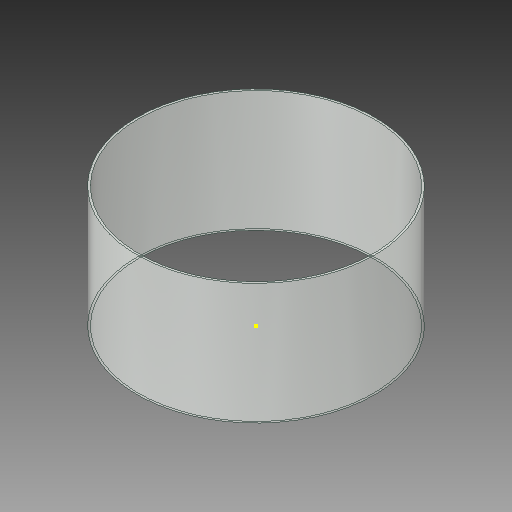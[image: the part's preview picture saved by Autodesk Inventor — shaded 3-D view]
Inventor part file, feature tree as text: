
AUTODESK INVENTOR PART (.ipt)
format: ipt  version: 2019 (Build 230136000, 136)  size: 118,272 bytes
history: native  units: mm
features: sketch x3, extrude x1
ambient origin geometry x8: Origin, YZ Plane, XZ Plane, XY Plane, X Axis, Y Axis, Z Axis, Center Point
bodies: Solid1 (feature_tree)
feature tree (4):
  sketch  "Sketch1"  dims[d0=305.0mm d1=300.0mm]
  extrude  "Extrusion1"  Depth=300.0mm
  sketch  "Sketch3"
  sketch  "Sketch2"  dims[d2=155.0mm d3=0.0mm]
